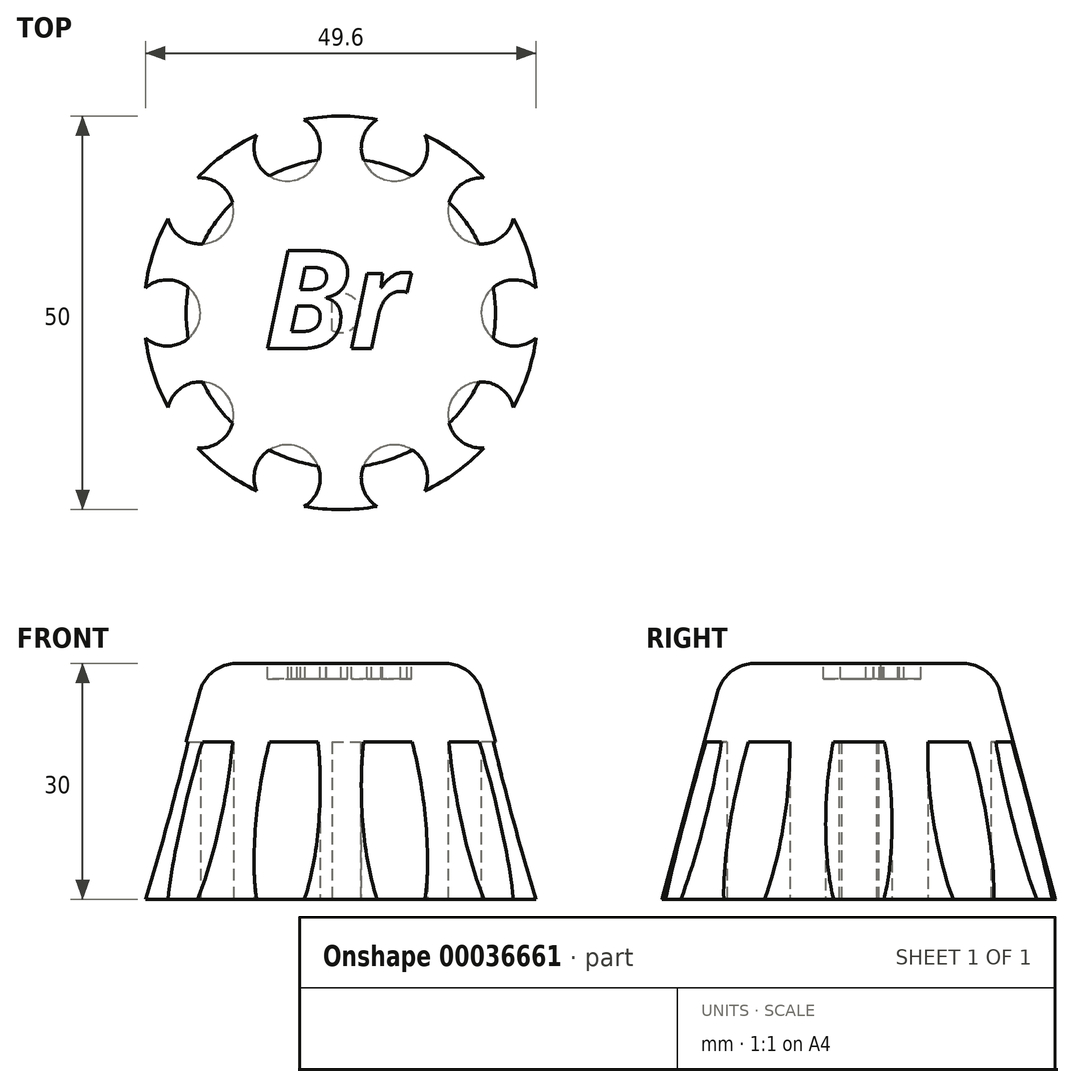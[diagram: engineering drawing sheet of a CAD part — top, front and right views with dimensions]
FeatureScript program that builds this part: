
annotation { "Feature Type Name" : "Feature", "Feature Type Description" : "" }
export const myFeature = defineFeature(function(context is Context, id is Id, definition is map)
    precondition{}
    {
        {
            var Q0;
            Q0=qCreatedBy(makeId("Top.planeOp"),FACE);
            var sketch = newSketch(context, id + "F0", { "sketchPlane" : qUnion([Q0])});
            skCircle(sketch, "E0", {"center": v(0, 0) * mm, "radius": 25 * mm});
            skSolve(sketch);
        }
        {
            var Q0;
            Q0 = qSketchRegion(id + "F0", true);
            extrude(context, id + "F1", {"entities" : qUnion([Q0]), "depth" : 30 * mm, "hasDraft" : true, "draftAngle" : 15 * degree, "draftPullDirection" : true});
        }
        {
            var Q0;
            Q0=qCreatedBy(makeId("Top.planeOp"),FACE);
            var sketch = newSketch(context, id + "F2", { "sketchPlane" : qUnion([Q0])});
            skArc(sketch, "E1", {"start": v(-1.13, -2.23) * mm, "mid": v(2.5, 0) * mm, "end": v(-1.13, 2.23) * mm});
            skLineSegment(sketch, "E2", {"start": v(-1.13, -2.23) * mm, "end": v(-1.13, 2.23) * mm});
            skSolve(sketch);
        }
        {
            var Q0;
            Q0 = qSketchRegion(id + "F2", true);
            extrude(context, id + "F3", {"entities" : qUnion([Q0]), "operationType" : NewBodyOperationType.REMOVE, "depth" : 20 * mm});
        }
        {
            var Q0;
            Q0=qCreatedBy(makeId("Top.planeOp"),FACE);
            var sketch = newSketch(context, id + "F4", { "sketchPlane" : qUnion([Q0])});
            skPoint(sketch, "E3.center", {"position": v(0, 0) * mm});
            skCircle(sketch, "E4", {"center": v(0, 0) * mm, "radius": 22.04 * mm, "construction": true});
            skCircle(sketch, "E5", {"center": v(22.04, 0) * mm, "radius": 4.2 * mm});
            skCircle(sketch, "E6.1.0", {"center": v(17.83, 12.96) * mm, "radius": 4.2 * mm});
            skCircle(sketch, "E6.2.0", {"center": v(6.81, 20.96) * mm, "radius": 4.2 * mm});
            skCircle(sketch, "E6.3.0", {"center": v(-6.81, 20.96) * mm, "radius": 4.2 * mm});
            skCircle(sketch, "E6.4.0", {"center": v(-17.83, 12.96) * mm, "radius": 4.2 * mm});
            skCircle(sketch, "E6.5.0", {"center": v(-22.04, 0) * mm, "radius": 4.2 * mm});
            skCircle(sketch, "E6.6.0", {"center": v(-17.83, -12.96) * mm, "radius": 4.2 * mm});
            skCircle(sketch, "E6.7.0", {"center": v(-6.81, -20.96) * mm, "radius": 4.2 * mm});
            skCircle(sketch, "E6.8.0", {"center": v(6.81, -20.96) * mm, "radius": 4.2 * mm});
            skCircle(sketch, "E6.9.0", {"center": v(17.83, -12.96) * mm, "radius": 4.2 * mm});
            skSolve(sketch);
        }
        {
            var Q0;
            Q0=makeQuery(id+"F1.opExtrude","CAP_EDGE",EDGE,{"disambiguationData":[OSD([sQuery(id+"F0.wireOp",EDGE,"E0")])],"isStart":false});
            fillet(context, id + "F5", {"entities" : qUnion([Q0]), "radius" : 5 * mm, "tangentPropagation" : true, "allowEdgeOverflow" : false});
        }
        {
            var Q0;
            Q0 = qSketchRegion(id + "F4", true);
            extrude(context, id + "F6", {"entities" : qUnion([Q0]), "operationType" : NewBodyOperationType.REMOVE, "depth" : 20 * mm});
        }
        {
            var Q0;
            Q0=makeQuery(id+"F1.opExtrude","CAP_FACE",FACE,{"disambiguationData":[OSD([sQuery(id+"F0.wireOp",EDGE,"E0")])],"isStart":false});
            var sketch = newSketch(context, id + "F7", { "sketchPlane" : qUnion([Q0])});
            skText(sketch, "E7", { "text": "Br", "fontName": "OpenSans-BoldItalic.ttf"});
            const initialGuessF7  = {"E7": [-0.00977, -0.00452, 1, 0, 0.01253]};
            skSetInitialGuess(sketch, initialGuessF7);
            skSolve(sketch);
        }
        {
            var Q0;
            Q0 = qSketchRegion(id + "F7", true);
            extrude(context, id + "F8", {"entities" : qUnion([Q0]), "operationType" : NewBodyOperationType.REMOVE, "oppositeDirection" : true, "depth" : 2 * mm});
        }
    });
